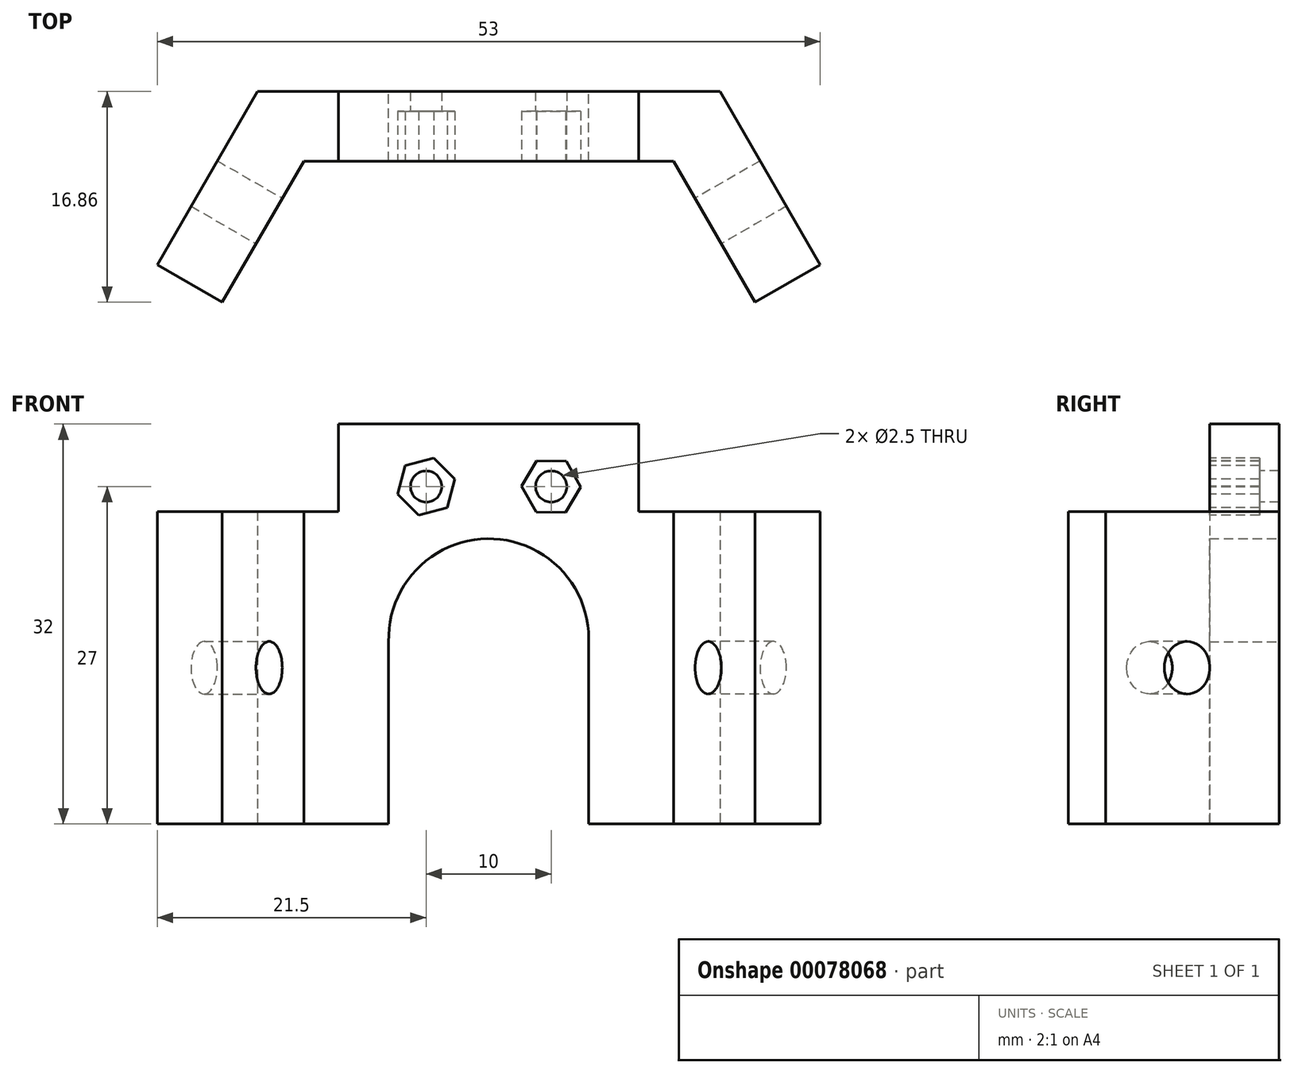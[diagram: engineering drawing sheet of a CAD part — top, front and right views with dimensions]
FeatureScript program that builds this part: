
annotation { "Feature Type Name" : "Feature", "Feature Type Description" : "" }
export const myFeature = defineFeature(function(context is Context, id is Id, definition is map)
    precondition{}
    {
        {
            var Q0;
            Q0=qCreatedBy(makeId("Top.planeOp"),FACE);
            var sketch = newSketch(context, id + "F0", { "sketchPlane" : qUnion([Q0])});
            skLineSegment(sketch, "E0", {"start": v(0, 0) * mm, "end": v(18.5, 0) * mm});
            skLineSegment(sketch, "E1", {"start": v(18.5, 0) * mm, "end": v(26.5, -13.86) * mm});
            skLineSegment(sketch, "E2", {"start": v(26.5, -13.86) * mm, "end": v(21.3, -16.86) * mm});
            skLineSegment(sketch, "E3", {"start": v(21.3, -16.86) * mm, "end": v(14.79, -5.57) * mm});
            skLineSegment(sketch, "E4", {"start": v(14.79, -5.57) * mm, "end": v(0, -5.57) * mm});
            skLineSegment(sketch, "E5.MirrorCS", {"start": v(-18.5, 0) * mm, "end": v(-26.5, -13.86) * mm});
            skLineSegment(sketch, "E6.MirrorCS", {"start": v(-26.5, -13.86) * mm, "end": v(-21.3, -16.86) * mm});
            skLineSegment(sketch, "E7.MirrorCS", {"start": v(-21.3, -16.86) * mm, "end": v(-14.79, -5.57) * mm});
            skLineSegment(sketch, "E8.MirrorCS", {"start": v(-14.79, -5.57) * mm, "end": v(0, -5.57) * mm});
            skLineSegment(sketch, "E9.MirrorCS", {"start": v(0, 0) * mm, "end": v(-18.5, 0) * mm});
            skSolve(sketch);
        }
        {
            var Q0;
            Q0=makeQuery(id+"F0.imprint","IMPRINT",FACE,{"disambiguationData":[TD([[makeQuery(id+"F0.imprint","IMPRINT",EDGE,{"derivedFrom":sQuery(id+"F0.wireOp",EDGE,"E0")}),-1.0]])]});
            extrude(context, id + "F1", {"entities" : qUnion([Q0]), "depth" : 25 * mm, "offsetDistance" : 25 * mm});
        }
        {
            var Q0;
            Q0=makeQuery(id+"F1.opExtrude","SWEPT_FACE",FACE,{"disambiguationData":[OSD([sQuery(id+"F0.wireOp",EDGE,"E5.MirrorCS")])]});
            var sketch = newSketch(context, id + "F2", { "sketchPlane" : qUnion([Q0])});
            skPoint(sketch, "E10", {"position": v(17.75, 12.5) * mm});
            skSolve(sketch);
        }
        {
            var Q0;
            Q0=sQuery(id+"F2.wireOp",VERTEX,"E10");
            var Q1;
            Q1=makeQuery(id+"F1.opExtrude","SWEPT_BODY",BODY,{"disambiguationData":[OSD([sQuery(id+"F0.wireOp",EDGE,"E0"),sQuery(id+"F0.wireOp",EDGE,"E1"),sQuery(id+"F0.wireOp",EDGE,"E2"),sQuery(id+"F0.wireOp",EDGE,"E3"),sQuery(id+"F0.wireOp",EDGE,"E4"),sQuery(id+"F0.wireOp",EDGE,"E5.MirrorCS"),sQuery(id+"F0.wireOp",EDGE,"E6.MirrorCS"),sQuery(id+"F0.wireOp",EDGE,"E7.MirrorCS"),sQuery(id+"F0.wireOp",EDGE,"E8.MirrorCS"),sQuery(id+"F0.wireOp",EDGE,"E9.MirrorCS")])]});
            hole(context, id + "F3", {"style" : HoleStyle.SIMPLE, "endStyle" : HoleEndStyle.THROUGH, "holeDiameter" : 4.2 * mm, "majorDiameter" : 5 * mm, "tappedDepth" : 12 * mm, "tapClearance" : 3, "locations" : qUnion([Q0]), "scope" : qUnion([Q1])});
        }
        {
            var Q0;
            Q0=makeQuery(id+"F1.opExtrude","SWEPT_FACE",FACE,{"disambiguationData":[OSD([sQuery(id+"F0.wireOp",EDGE,"E1")])]});
            var sketch = newSketch(context, id + "F4", { "sketchPlane" : qUnion([Q0])});
            skPoint(sketch, "E11", {"position": v(-17.75, 12.5) * mm});
            skSolve(sketch);
        }
        {
            var Q0;
            Q0=sQuery(id+"F4.wireOp",VERTEX,"E11");
            var Q1;
            Q1=makeQuery(id+"F1.opExtrude","SWEPT_BODY",BODY,{"disambiguationData":[OSD([sQuery(id+"F0.wireOp",EDGE,"E0"),sQuery(id+"F0.wireOp",EDGE,"E1"),sQuery(id+"F0.wireOp",EDGE,"E2"),sQuery(id+"F0.wireOp",EDGE,"E3"),sQuery(id+"F0.wireOp",EDGE,"E4"),sQuery(id+"F0.wireOp",EDGE,"E5.MirrorCS"),sQuery(id+"F0.wireOp",EDGE,"E6.MirrorCS"),sQuery(id+"F0.wireOp",EDGE,"E7.MirrorCS"),sQuery(id+"F0.wireOp",EDGE,"E8.MirrorCS"),sQuery(id+"F0.wireOp",EDGE,"E9.MirrorCS")])]});
            hole(context, id + "F5", {"style" : HoleStyle.SIMPLE, "endStyle" : HoleEndStyle.THROUGH, "holeDiameter" : 4.2 * mm, "majorDiameter" : 5 * mm, "tappedDepth" : 12 * mm, "tapClearance" : 3, "locations" : qUnion([Q0]), "scope" : qUnion([Q1])});
        }
        {
            var Q0;
            Q0=makeQuery(id+"F1.opExtrude","CAP_FACE",FACE,{"disambiguationData":[OSD([sQuery(id+"F0.wireOp",EDGE,"E0"),sQuery(id+"F0.wireOp",EDGE,"E1"),sQuery(id+"F0.wireOp",EDGE,"E2"),sQuery(id+"F0.wireOp",EDGE,"E3"),sQuery(id+"F0.wireOp",EDGE,"E4"),sQuery(id+"F0.wireOp",EDGE,"E5.MirrorCS"),sQuery(id+"F0.wireOp",EDGE,"E6.MirrorCS"),sQuery(id+"F0.wireOp",EDGE,"E7.MirrorCS"),sQuery(id+"F0.wireOp",EDGE,"E8.MirrorCS"),sQuery(id+"F0.wireOp",EDGE,"E9.MirrorCS")])],"isStart":false});
            var sketch = newSketch(context, id + "F6", { "sketchPlane" : qUnion([Q0])});
            skLineSegment(sketch, "E12", {"start": v(0, 0) * mm, "end": v(12, 0) * mm});
            skLineSegment(sketch, "E13", {"start": v(12, 0) * mm, "end": v(12, -5.57) * mm});
            skLineSegment(sketch, "E14", {"start": v(12, -5.57) * mm, "end": v(-12, -5.57) * mm});
            skLineSegment(sketch, "E15", {"start": v(-12, -5.57) * mm, "end": v(-12, 0) * mm});
            skLineSegment(sketch, "E16", {"start": v(-12, 0) * mm, "end": v(0, 0) * mm});
            skSolve(sketch);
        }
        {
            var Q0;
            Q0 = qSketchRegion(id + "F6", true);
            var Q1;
            Q1=makeQuery(id+"F6.imprint","IMPRINT",FACE,{"disambiguationData":[TD([[makeQuery(id+"F6.imprint","IMPRINT",EDGE,{"derivedFrom":sQuery(id+"F6.wireOp",EDGE,"E12")}),-1.0]])]});
            extrude(context, id + "F7", {"entities" : qUnion([Q0, Q1]), "operationType" : NewBodyOperationType.ADD, "depth" : 7 * mm, "offsetDistance" : 25 * mm});
        }
        {
            var Q0;
            Q0=makeQuery(id+"F7.boolean.opBoolean","MERGE",FACE,{"derivedFrom":[makeQuery(id+"F1.opExtrude","SWEPT_FACE",FACE,{"disambiguationData":[OSD([sQuery(id+"F0.wireOp",EDGE,"E0"),sQuery(id+"F0.wireOp",EDGE,"E9.MirrorCS")])]}),makeQuery(id+"F7.opExtrude","SWEPT_FACE",FACE,{"disambiguationData":[OSD([sQuery(id+"F6.wireOp",EDGE,"E12"),sQuery(id+"F6.wireOp",EDGE,"E16")])]})]});
            var sketch = newSketch(context, id + "F8", { "sketchPlane" : qUnion([Q0])});
            skArc(sketch, "E17", {"start": v(8, 14.58) * mm, "mid": v(0.12, 22.82) * mm, "end": v(-8, 14.82) * mm});
            skLineSegment(sketch, "E18", {"start": v(8, 14.58) * mm, "end": v(8, 0) * mm});
            skLineSegment(sketch, "E19", {"start": v(8, 0) * mm, "end": v(-8, 0) * mm});
            skLineSegment(sketch, "E20", {"start": v(-8, 0) * mm, "end": v(-8, 14.82) * mm});
            skSolve(sketch);
        }
        {
            var Q0;
            Q0 = qSketchRegion(id + "F8", true);
            extrude(context, id + "F9", {"entities" : qUnion([Q0]), "operationType" : NewBodyOperationType.REMOVE, "oppositeDirection" : true, "depth" : 25 * mm, "offsetDistance" : 25 * mm});
        }
        {
            var Q0;
            Q0=makeQuery(id+"F7.boolean.opBoolean","MERGE",FACE,{"derivedFrom":[makeQuery(id+"F1.opExtrude","SWEPT_FACE",FACE,{"disambiguationData":[OSD([sQuery(id+"F0.wireOp",EDGE,"E0"),sQuery(id+"F0.wireOp",EDGE,"E9.MirrorCS")])]}),makeQuery(id+"F7.opExtrude","SWEPT_FACE",FACE,{"disambiguationData":[OSD([sQuery(id+"F6.wireOp",EDGE,"E12"),sQuery(id+"F6.wireOp",EDGE,"E16")])]})]});
            var sketch = newSketch(context, id + "F10", { "sketchPlane" : qUnion([Q0])});
            skPoint(sketch, "E21", {"position": v(-5, 27) * mm});
            skPoint(sketch, "E22.MirrorP", {"position": v(5, 27) * mm});
            skSolve(sketch);
        }
        {
            var Q0;
            Q0=sQuery(id+"F10.wireOp",VERTEX,"E22.MirrorP");
            var Q1;
            Q1=sQuery(id+"F10.wireOp",VERTEX,"E21");
            var Q2;
            Q2=makeQuery(id+"F1.opExtrude","SWEPT_BODY",BODY,{"disambiguationData":[OSD([sQuery(id+"F0.wireOp",EDGE,"E0"),sQuery(id+"F0.wireOp",EDGE,"E1"),sQuery(id+"F0.wireOp",EDGE,"E2"),sQuery(id+"F0.wireOp",EDGE,"E3"),sQuery(id+"F0.wireOp",EDGE,"E4"),sQuery(id+"F0.wireOp",EDGE,"E5.MirrorCS"),sQuery(id+"F0.wireOp",EDGE,"E6.MirrorCS"),sQuery(id+"F0.wireOp",EDGE,"E7.MirrorCS"),sQuery(id+"F0.wireOp",EDGE,"E8.MirrorCS"),sQuery(id+"F0.wireOp",EDGE,"E9.MirrorCS")])]});
            hole(context, id + "F11", {"style" : HoleStyle.SIMPLE, "endStyle" : HoleEndStyle.THROUGH, "holeDiameter" : 2.5 * mm, "majorDiameter" : 5 * mm, "tappedDepth" : 12 * mm, "tapClearance" : 3, "locations" : qUnion([Q0, Q1]), "scope" : qUnion([Q2])});
        }
        {
            var Q0;
            Q0=makeQuery(id+"F7.boolean.opBoolean","MERGE",FACE,{"derivedFrom":[makeQuery(id+"F1.opExtrude","SWEPT_FACE",FACE,{"disambiguationData":[OSD([sQuery(id+"F0.wireOp",EDGE,"E4"),sQuery(id+"F0.wireOp",EDGE,"E8.MirrorCS")])]}),makeQuery(id+"F7.opExtrude","SWEPT_FACE",FACE,{"disambiguationData":[OSD([sQuery(id+"F6.wireOp",EDGE,"E14")])]})]});
            var sketch = newSketch(context, id + "F12", { "sketchPlane" : qUnion([Q0])});
            skCircle(sketch, "E23.cCircle", {"center": v(-5, 27) * mm, "radius": 2.05 * mm, "construction": true});
            skLineSegment(sketch, "E23.0", {"start": v(-3.33, 25.32) * mm, "end": v(-5.61, 24.71) * mm});
            skLineSegment(sketch, "E23.1", {"start": v(-5.61, 24.71) * mm, "end": v(-7.29, 26.39) * mm});
            skLineSegment(sketch, "E23.2", {"start": v(-7.29, 26.39) * mm, "end": v(-6.67, 28.68) * mm});
            skLineSegment(sketch, "E23.3", {"start": v(-6.67, 28.68) * mm, "end": v(-4.39, 29.29) * mm});
            skLineSegment(sketch, "E23.4", {"start": v(-4.39, 29.29) * mm, "end": v(-2.71, 27.61) * mm});
            skLineSegment(sketch, "E23.5", {"start": v(-2.71, 27.61) * mm, "end": v(-3.33, 25.32) * mm});
            skPoint(sketch, "E23.0.midPoint", {"position": v(-4.47, 25.02) * mm});
            skCircle(sketch, "E24.cCircle", {"center": v(5, 27) * mm, "radius": 2.05 * mm, "construction": true});
            skLineSegment(sketch, "E24.0", {"start": v(7.37, 26.97) * mm, "end": v(6.16, 24.94) * mm});
            skLineSegment(sketch, "E24.1", {"start": v(6.16, 24.94) * mm, "end": v(3.8, 24.96) * mm});
            skLineSegment(sketch, "E24.2", {"start": v(3.8, 24.96) * mm, "end": v(2.63, 27.03) * mm});
            skLineSegment(sketch, "E24.3", {"start": v(2.63, 27.03) * mm, "end": v(3.84, 29.06) * mm});
            skLineSegment(sketch, "E24.4", {"start": v(3.84, 29.06) * mm, "end": v(6.2, 29.04) * mm});
            skLineSegment(sketch, "E24.5", {"start": v(6.2, 29.04) * mm, "end": v(7.37, 26.97) * mm});
            skPoint(sketch, "E24.0.midPoint", {"position": v(6.76, 25.95) * mm});
            skSolve(sketch);
        }
        {
            var Q0;
            Q0 = qSketchRegion(id + "F12", true);
            extrude(context, id + "F13", {"entities" : qUnion([Q0]), "operationType" : NewBodyOperationType.REMOVE, "oppositeDirection" : true, "depth" : 4 * mm, "offsetDistance" : 25 * mm});
        }
    });
